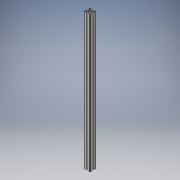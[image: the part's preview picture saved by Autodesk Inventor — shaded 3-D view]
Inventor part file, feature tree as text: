
AUTODESK INVENTOR PART (.ipt)
format: ipt  version: 2016 (Build 200138000, 138)  size: 1,060,352 bytes
history: native  units: in
note: dims shown in document units (in); Inventor stores cm internally (conversion verified against a paired STEP export)
features: extrude x1, sketch x1
ambient origin geometry x8: Origin, YZ Plane, XZ Plane, XY Plane, X Axis, Y Axis, Z Axis, Center Point
bodies: Solid1 (feature_tree)
feature tree (2):
  extrude  "Extrusion1"  [1 undecoded]
  sketch  "Sketch1"  dims[d0=26.7717in d1=0.0in]
note: 1 required parameter value undecoded (feature->parameter linkage not recoverable at this tier; creation-order binding heuristic only, values carry confidence <= 0.55)
